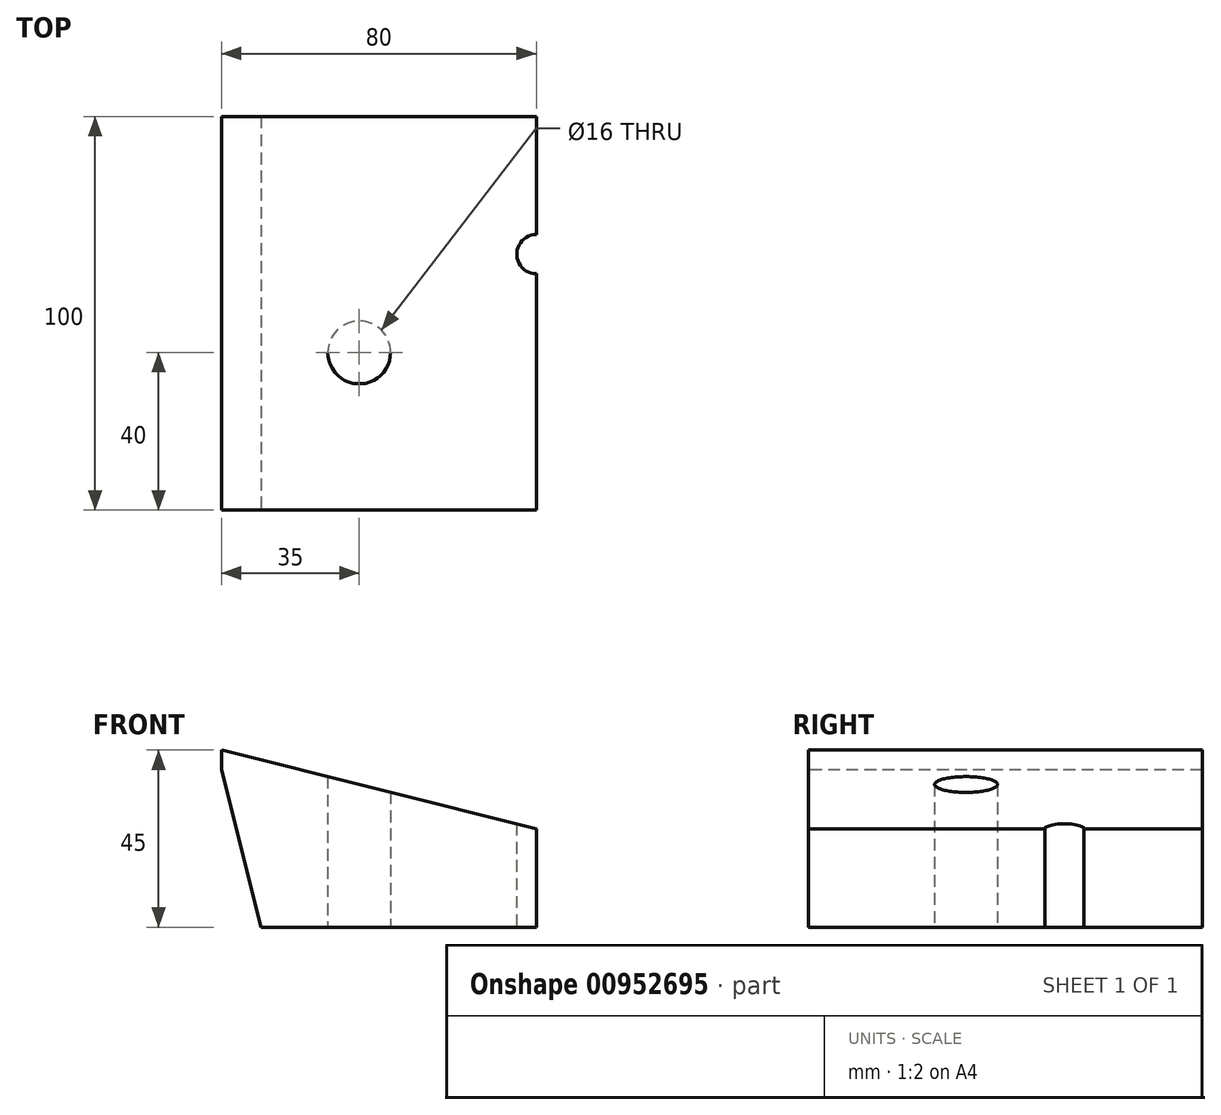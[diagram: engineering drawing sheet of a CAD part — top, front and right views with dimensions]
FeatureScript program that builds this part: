
annotation { "Feature Type Name" : "Feature", "Feature Type Description" : "" }
export const myFeature = defineFeature(function(context is Context, id is Id, definition is map)
    precondition{}
    {
        {
            var Q0;
            Q0=qCreatedBy(makeId("Front.planeOp"),FACE);
            var sketch = newSketch(context, id + "F0", { "sketchPlane" : qUnion([Q0])});
            skLineSegment(sketch, "E0", {"start": v(0, 0) * mm, "end": v(-10, 40) * mm});
            skLineSegment(sketch, "E1", {"start": v(-10, 40) * mm, "end": v(-10, 45) * mm});
            skLineSegment(sketch, "E2", {"start": v(-10, 45) * mm, "end": v(70, 25) * mm});
            skLineSegment(sketch, "E3", {"start": v(70, 25) * mm, "end": v(70, 0) * mm});
            skLineSegment(sketch, "E4", {"start": v(70, 0) * mm, "end": v(0, 0) * mm});
            skSolve(sketch);
        }
        {
            var Q0;
            Q0=makeQuery(id+"F0.imprint","IMPRINT",FACE,{"disambiguationData":[TD([[makeQuery(id+"F0.imprint","IMPRINT",EDGE,{"derivedFrom":sQuery(id+"F0.wireOp",EDGE,"E0")}),-1.0]])]});
            extrude(context, id + "F1", {"entities" : qUnion([Q0]), "oppositeDirection" : true, "depth" : 100 * mm, "offsetDistance" : 25 * mm});
        }
        {
            var Q0;
            Q0=makeQuery(id+"F1.opExtrude","SWEPT_FACE",FACE,{"disambiguationData":[OSD([sQuery(id+"F0.wireOp",EDGE,"E4")])]});
            var sketch = newSketch(context, id + "F2", { "sketchPlane" : qUnion([Q0])});
            skCircle(sketch, "E5", {"center": v(25, -40) * mm, "radius": 8 * mm});
            skSolve(sketch);
        }
        {
            var Q0;
            Q0 = qSketchRegion(id + "F2", true);
            extrude(context, id + "F3", {"entities" : qUnion([Q0]), "operationType" : NewBodyOperationType.REMOVE, "endBound" : BoundingType.THROUGH_ALL, "oppositeDirection" : true, "depth" : 25 * mm, "offsetDistance" : 25 * mm});
        }
        {
            var Q0;
            Q0=makeQuery(id+"F1.opExtrude","SWEPT_FACE",FACE,{"disambiguationData":[OSD([sQuery(id+"F0.wireOp",EDGE,"E4")])]});
            var sketch = newSketch(context, id + "F4", { "sketchPlane" : qUnion([Q0])});
            skCircle(sketch, "E6", {"center": v(70, -65) * mm, "radius": 5 * mm});
            skSolve(sketch);
        }
        {
            var Q0;
            Q0 = qSketchRegion(id + "F4", true);
            extrude(context, id + "F5", {"entities" : qUnion([Q0]), "operationType" : NewBodyOperationType.REMOVE, "endBound" : BoundingType.THROUGH_ALL, "oppositeDirection" : true, "depth" : 25 * mm, "offsetDistance" : 25 * mm});
        }
    });
